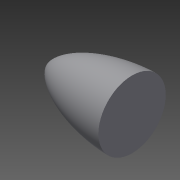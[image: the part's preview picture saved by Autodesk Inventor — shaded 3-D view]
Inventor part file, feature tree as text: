
AUTODESK INVENTOR PART (.ipt)
format: ipt  version: 2014 SP1 (Build 180222100, 222)  size: 132,608 bytes
history: native  units: mm
features: revolve x1, sketch x1
ambient origin geometry x8: Origin, YZ Plane, XZ Plane, XY Plane, X Axis, Y Axis, Z Axis, Center Point
bodies: Solid1 (feature_tree)
feature tree (2):
  revolve  "Revolution1"  [1 undecoded]
  sketch  "Sketch1"  dims[d0=100.0mm d1=40.0mm d2=90.0deg]
note: 1 required parameter value undecoded (feature->parameter linkage not recoverable at this tier; creation-order binding heuristic only, values carry confidence <= 0.55)
